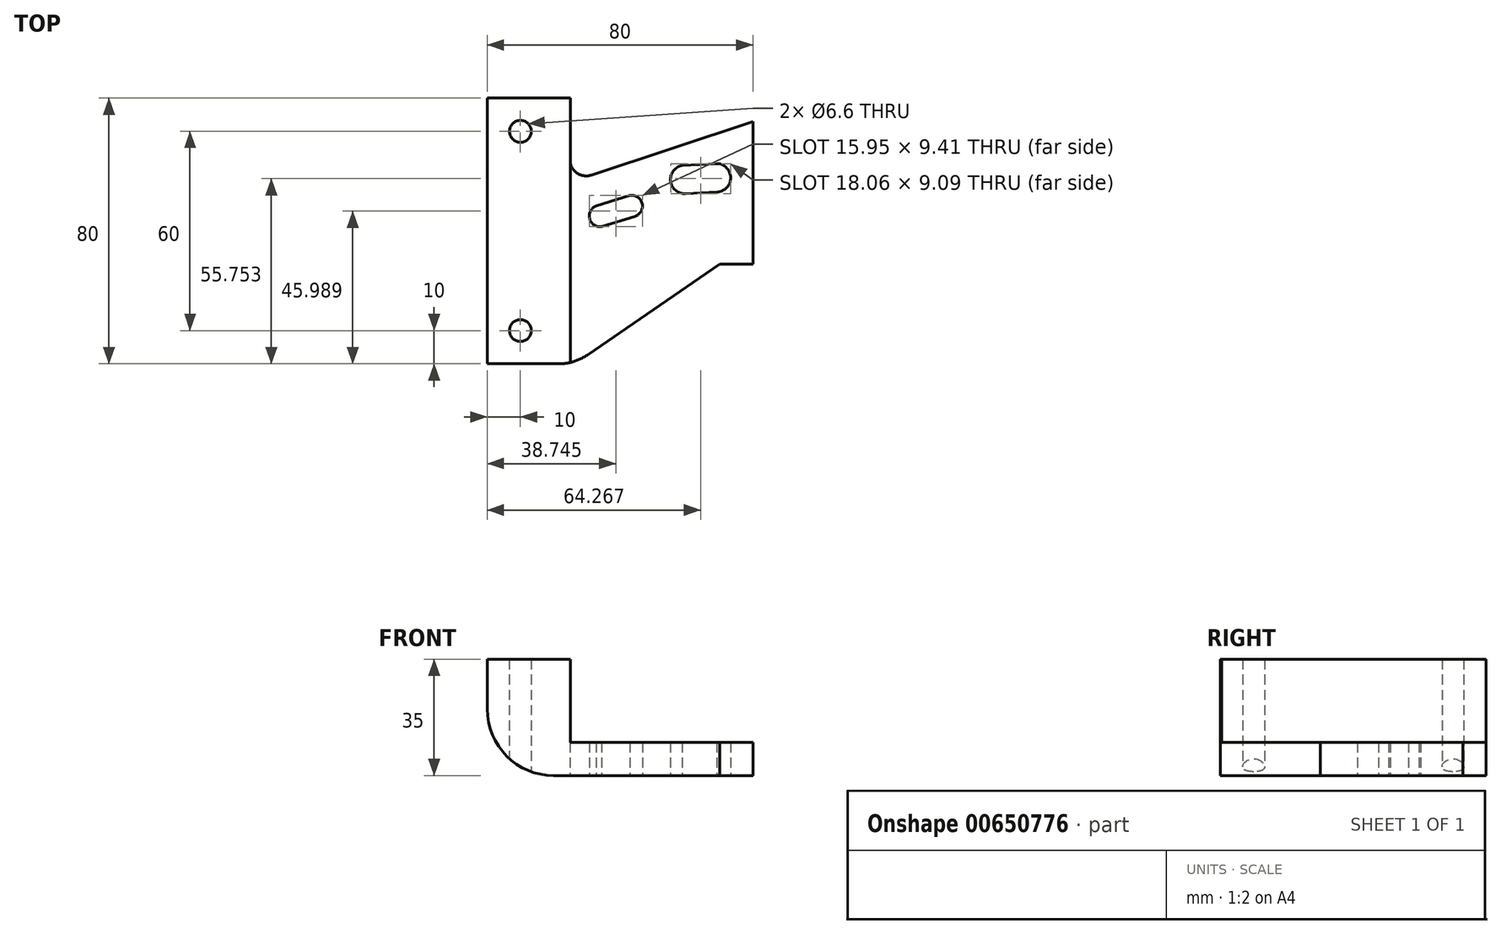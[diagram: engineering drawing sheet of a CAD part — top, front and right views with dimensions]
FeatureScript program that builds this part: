
annotation { "Feature Type Name" : "Feature", "Feature Type Description" : "" }
export const myFeature = defineFeature(function(context is Context, id is Id, definition is map)
    precondition{}
    {
        {
            var Q0;
            Q0=qCreatedBy(makeId("Front.planeOp"),FACE);
            var sketch = newSketch(context, id + "F0", { "sketchPlane" : qUnion([Q0])});
            skLineSegment(sketch, "E0", {"start": v(0, 0) * mm, "end": v(25, 0) * mm});
            skLineSegment(sketch, "E1", {"start": v(25, 0) * mm, "end": v(25, -30) * mm});
            skLineSegment(sketch, "E2", {"start": v(25, -30) * mm, "end": v(70, -30) * mm});
            skLineSegment(sketch, "E3.0", {"start": v(20, -35) * mm, "end": v(70, -35) * mm});
            skLineSegment(sketch, "E3.1", {"start": v(20, -5) * mm, "end": v(20, -35) * mm});
            skLineSegment(sketch, "E3.2", {"start": v(0, -5) * mm, "end": v(20, -5) * mm});
            skLineSegment(sketch, "E4", {"start": v(0, 0) * mm, "end": v(0, -5) * mm});
            skLineSegment(sketch, "E5", {"start": v(70, -30) * mm, "end": v(70, -35) * mm});
            skSolve(sketch);
        }
        {
            var Q0;
            Q0=makeQuery(id+"F0.imprint","IMPRINT",FACE,{"disambiguationData":[TD([[makeQuery(id+"F0.imprint","IMPRINT",EDGE,{"derivedFrom":sQuery(id+"F0.wireOp",EDGE,"E0")}),-1.0]])]});
            extrude(context, id + "F1", {"entities" : qUnion([Q0]), "depth" : 80 * mm, "offsetDistance" : 25 * mm});
        }
        {
            var Q0;
            Q0=makeQuery(id+"F1.opExtrude","SWEPT_FACE",FACE,{"disambiguationData":[OSD([sQuery(id+"F0.wireOp",EDGE,"E3.2")])]});
            var sketch = newSketch(context, id + "F2", { "sketchPlane" : qUnion([Q0])});
            skCircle(sketch, "E6", {"center": v(10, 70) * mm, "radius": 3.3 * mm});
            skCircle(sketch, "E7", {"center": v(10, 10) * mm, "radius": 3.3 * mm});
            skSolve(sketch);
        }
        {
            var Q0;
            Q0=makeQuery(id+"F2.imprint","IMPRINT",FACE,{"disambiguationData":[TD([[makeQuery(id+"F2.imprint","IMPRINT",EDGE,{"derivedFrom":sQuery(id+"F2.wireOp",EDGE,"E6")}),1.0]])]});
            var Q1;
            Q1=makeQuery(id+"F2.imprint","IMPRINT",FACE,{"disambiguationData":[TD([[makeQuery(id+"F2.imprint","IMPRINT",EDGE,{"derivedFrom":sQuery(id+"F2.wireOp",EDGE,"E7")}),1.0]])]});
            extrude(context, id + "F3", {"entities" : qUnion([Q0, Q1]), "operationType" : NewBodyOperationType.REMOVE, "oppositeDirection" : true, "depth" : 25 * mm, "offsetDistance" : 25 * mm});
        }
        {
            var Q0;
            Q0=makeQuery(id+"F1.opExtrude","SWEPT_FACE",FACE,{"disambiguationData":[OSD([sQuery(id+"F0.wireOp",EDGE,"E3.0")])]});
            var sketch = newSketch(context, id + "F4", { "sketchPlane" : qUnion([Q0])});
            skLineSegment(sketch, "E8", {"start": v(70, 50) * mm, "end": v(26.25, 80) * mm});
            skLineSegment(sketch, "E9", {"start": v(26.25, 80) * mm, "end": v(70, 80) * mm});
            skLineSegment(sketch, "E10", {"start": v(70, 80) * mm, "end": v(70, 50) * mm});
            skSolve(sketch);
        }
        {
            var Q0;
            Q0=makeQuery(id+"F4.imprint","IMPRINT",FACE,{"disambiguationData":[TD([[makeQuery(id+"F4.imprint","IMPRINT",EDGE,{"derivedFrom":sQuery(id+"F4.wireOp",EDGE,"E8")}),-1.0]])]});
            extrude(context, id + "F5", {"entities" : qUnion([Q0]), "operationType" : NewBodyOperationType.REMOVE, "oppositeDirection" : true, "depth" : 25 * mm, "offsetDistance" : 25 * mm});
        }
        {
            var Q0;
            Q0=makeQuery(id+"F1.opExtrude","SWEPT_FACE",FACE,{"disambiguationData":[OSD([sQuery(id+"F0.wireOp",EDGE,"E3.0")])]});
            var sketch = newSketch(context, id + "F6", { "sketchPlane" : qUnion([Q0])});
            skArc(sketch, "E11", {"start": v(68.41, 19.74) * mm, "mid": v(73.28, 23.6) * mm, "end": v(69.23, 28.3) * mm});
            skArc(sketch, "E12", {"start": v(59.75, 28.8) * mm, "mid": v(55.2, 24.45) * mm, "end": v(59.86, 20.22) * mm});
            skArc(sketch, "E13", {"start": v(42.16, 29.54) * mm, "mid": v(46.54, 31.34) * mm, "end": v(44.47, 35.6) * mm});
            skArc(sketch, "E14", {"start": v(35.45, 38.4) * mm, "mid": v(30.95, 36.62) * mm, "end": v(33.22, 32.34) * mm});
            skLineSegment(sketch, "E15", {"start": v(34.45, 38.72) * mm, "end": v(44.47, 35.6) * mm});
            skLineSegment(sketch, "E16", {"start": v(32.83, 32.47) * mm, "end": v(42.9, 29.3) * mm});
            skLineSegment(sketch, "E17", {"start": v(59.75, 28.8) * mm, "end": v(69.23, 28.3) * mm});
            skLineSegment(sketch, "E18", {"start": v(58.67, 20.28) * mm, "end": v(69.11, 19.7) * mm});
            skSolve(sketch);
        }
        {
            var Q0;
            Q0=makeQuery(id+"F1.opExtrude","SWEPT_FACE",FACE,{"disambiguationData":[OSD([sQuery(id+"F0.wireOp",EDGE,"E5")])]});
            var sketch = newSketch(context, id + "F7", { "sketchPlane" : qUnion([Q0])});
            skLineSegment(sketch, "E19.bottom", {"start": v(-50, -35) * mm, "end": v(0, -35) * mm});
            skLineSegment(sketch, "E19.top", {"start": v(-50, -30) * mm, "end": v(0, -30) * mm});
            skLineSegment(sketch, "E19.left", {"start": v(-50, -35) * mm, "end": v(-50, -30) * mm});
            skLineSegment(sketch, "E19.right", {"start": v(0, -35) * mm, "end": v(0, -30) * mm});
            skSolve(sketch);
        }
        {
            var Q0;
            Q0=makeQuery(id+"F7.imprint","IMPRINT",FACE,{"disambiguationData":[TD([[makeQuery(id+"F7.imprint","IMPRINT",EDGE,{"derivedFrom":sQuery(id+"F7.wireOp",EDGE,"E19.bottom")}),1.0]])]});
            extrude(context, id + "F8", {"entities" : qUnion([Q0]), "operationType" : NewBodyOperationType.ADD, "depth" : 10 * mm, "offsetDistance" : 25 * mm});
        }
        {
            var Q0;
            {var subQ0=sQuery(id+"F6.wireOp",EDGE,"E15");var subQ6=sQuery(id+"F6.wireOp",EDGE,"E13");var subQ7=makeQuery(id+"F6.imprint","INTERSECT",VERTEX,{"derivedFrom":[subQ6,subQ0]});Q0=makeQuery(id+"F6.imprint","IMPRINT",FACE,{"disambiguationData":[TD([[makeQuery(id+"F6.imprint","IMPRINT",EDGE,{"disambiguationData":[TD([[subQ7,1.0]])],"derivedFrom":subQ6}),1.0]])]});}
            var Q1;
            {var subQ0=sQuery(id+"F6.wireOp",EDGE,"E17");Q1=makeQuery(id+"F6.imprint","IMPRINT",FACE,{"disambiguationData":[TD([[makeQuery(id+"F6.imprint","IMPRINT",EDGE,{"derivedFrom":subQ0}),-1.0]])]});}
            var Q2;
            {var subQ0=sQuery(id+"F6.wireOp",EDGE,"E11");var subQ1=makeQuery(id+"F1.opExtrude","SWEPT_EDGE",EDGE,{"disambiguationData":[OSD([sQuery(id+"F0.wireOp",EDGE,"E3.0"),sQuery(id+"F0.wireOp",EDGE,"E5")])]});var subQ2=makeQuery(id+"F6.imprint","INTERSECT",VERTEX,{"disambiguationData":[OD(0.0)],"derivedFrom":[subQ1,subQ0]});Q2=makeQuery(id+"F6.imprint","IMPRINT",FACE,{"disambiguationData":[TD([[makeQuery(id+"F6.imprint","IMPRINT",EDGE,{"disambiguationData":[TD([[subQ2,-1.0]])],"derivedFrom":subQ0}),1.0]])]});}
            extrude(context, id + "F9", {"entities" : qUnion([Q0, Q1, Q2]), "operationType" : NewBodyOperationType.REMOVE, "oppositeDirection" : true, "depth" : 25 * mm, "offsetDistance" : 25 * mm});
        }
        {
            var Q0;
            Q0=makeQuery(id+"F8.boolean.opBoolean","MERGE",FACE,{"derivedFrom":[makeQuery(id+"F1.opExtrude","SWEPT_FACE",FACE,{"disambiguationData":[OSD([sQuery(id+"F0.wireOp",EDGE,"E3.0")])]}),makeQuery(id+"F8.opExtrude","SWEPT_FACE",FACE,{"disambiguationData":[OSD([sQuery(id+"F7.wireOp",EDGE,"E19.bottom")])]})]});
            var sketch = newSketch(context, id + "F10", { "sketchPlane" : qUnion([Q0])});
            skLineSegment(sketch, "E20", {"start": v(31.46, 23.18) * mm, "end": v(80, 7) * mm});
            skLineSegment(sketch, "E21", {"start": v(24.88, 0) * mm, "end": v(24.88, 18.44) * mm});
            skLineSegment(sketch, "E22", {"start": v(80, 7) * mm, "end": v(80, 0) * mm});
            skLineSegment(sketch, "E23", {"start": v(80, 0) * mm, "end": v(24.88, 0) * mm});
            skPoint(sketch, "E24.orphan", {"position": v(20, 27) * mm});
            skPoint(sketch, "E25.visualSharp", {"position": v(24.88, 25.37) * mm});
            skArc(sketch, "E25.filletArc", {"start": v(31.46, 23.18) * mm, "mid": v(26.96, 22.5) * mm, "end": v(24.88, 18.44) * mm});
            skSolve(sketch);
        }
        {
            var Q0;
            Q0=makeQuery(id+"F1.opExtrude","SWEPT_FACE",FACE,{"disambiguationData":[OSD([sQuery(id+"F0.wireOp",EDGE,"E3.2")])]});
            var sketch = newSketch(context, id + "F11", { "sketchPlane" : qUnion([Q0])});
            skLineSegment(sketch, "E26.bottom", {"start": v(0, 80) * mm, "end": v(20, 80) * mm});
            skLineSegment(sketch, "E26.top", {"start": v(0, 0) * mm, "end": v(20, 0) * mm});
            skLineSegment(sketch, "E26.left", {"start": v(0, 80) * mm, "end": v(0, 0) * mm});
            skLineSegment(sketch, "E26.right", {"start": v(20, 80) * mm, "end": v(20, 0) * mm});
            skSolve(sketch);
        }
        {
            var Q0;
            Q0=makeQuery(id+"F11.imprint","IMPRINT",FACE,{"disambiguationData":[TD([[makeQuery(id+"F11.imprint","IMPRINT",EDGE,{"derivedFrom":sQuery(id+"F11.wireOp",EDGE,"E26.bottom")}),-1.0]])]});
            extrude(context, id + "F12", {"entities" : qUnion([Q0]), "operationType" : NewBodyOperationType.ADD, "depth" : 30 * mm, "offsetDistance" : 25 * mm});
        }
        {
            var Q0;
            Q0=makeQuery(id+"F12.opExtrude","CAP_EDGE",EDGE,{"disambiguationData":[OSD([sQuery(id+"F11.wireOp",EDGE,"E26.left")])],"isStart":false});
            fillet(context, id + "F13", {"entities" : qUnion([Q0]), "radius" : 20 * mm, "tangentPropagation" : true, "allowEdgeOverflow" : false});
        }
        {
            var Q0;
            Q0=makeQuery(id+"F8.boolean.opBoolean","MERGE",FACE,{"derivedFrom":[makeQuery(id+"F1.opExtrude","SWEPT_FACE",FACE,{"disambiguationData":[OSD([sQuery(id+"F0.wireOp",EDGE,"E2")])]}),makeQuery(id+"F8.opExtrude","SWEPT_FACE",FACE,{"disambiguationData":[OSD([sQuery(id+"F7.wireOp",EDGE,"E19.top")])]})]});
            var sketch = newSketch(context, id + "F14", { "sketchPlane" : qUnion([Q0])});
            skLineSegment(sketch, "E27", {"start": v(25, 0) * mm, "end": v(80, 0) * mm});
            skLineSegment(sketch, "E28", {"start": v(80, 0) * mm, "end": v(80, -47.85) * mm});
            skLineSegment(sketch, "E29", {"start": v(80, -47.85) * mm, "end": v(80, -50) * mm});
            skLineSegment(sketch, "E30", {"start": v(80, -50) * mm, "end": v(70, -50) * mm});
            skLineSegment(sketch, "E31", {"start": v(70, -50) * mm, "end": v(26.25, -80) * mm});
            skLineSegment(sketch, "E32", {"start": v(26.25, -80) * mm, "end": v(25, -80) * mm});
            skLineSegment(sketch, "E33", {"start": v(25, -80) * mm, "end": v(25, 0) * mm});
            skSolve(sketch);
        }
        {
            var Q0;
            Q0=makeQuery(id+"F14.imprint","IMPRINT",FACE,{"disambiguationData":[TD([[makeQuery(id+"F14.imprint","IMPRINT",EDGE,{"derivedFrom":sQuery(id+"F14.wireOp",EDGE,"E27")}),-1.0]])]});
            extrude(context, id + "F15", {"entities" : qUnion([Q0]), "operationType" : NewBodyOperationType.ADD, "depth" : 5 * mm, "offsetDistance" : 25 * mm});
        }
        {
            var Q0;
            Q0=makeQuery(id+"F10.imprint","IMPRINT",FACE,{"disambiguationData":[TD([[makeQuery(id+"F10.imprint","IMPRINT",EDGE,{"derivedFrom":sQuery(id+"F10.wireOp",EDGE,"E20")}),-1.0]])]});
            extrude(context, id + "F16", {"entities" : qUnion([Q0]), "operationType" : NewBodyOperationType.REMOVE, "oppositeDirection" : true, "depth" : 10 * mm, "offsetDistance" : 25 * mm});
        }
        {
            var Q0;
            Q0=makeQuery(id+"F15.boolean.opBoolean","MERGE",EDGE,{"derivedFrom":[makeQuery(id+"F5.boolean.opBoolean","COPY",EDGE,{"derivedFrom":makeQuery(id+"F5.opExtrude","SWEPT_EDGE",EDGE,{"disambiguationData":[OSD([sQuery(id+"F0.wireOp",EDGE,"E3.0"),sQuery(id+"F4.wireOp",EDGE,"E8"),sQuery(id+"F4.wireOp",EDGE,"E9")])]})}),makeQuery(id+"F15.opExtrude","SWEPT_EDGE",EDGE,{"disambiguationData":[OSD([sQuery(id+"F14.wireOp",EDGE,"E31"),sQuery(id+"F14.wireOp",EDGE,"E32")])]})]});
            fillet(context, id + "F17", {"entities" : qUnion([Q0]), "radius" : 15 * mm, "tangentPropagation" : true, "allowEdgeOverflow" : false});
        }
    });
